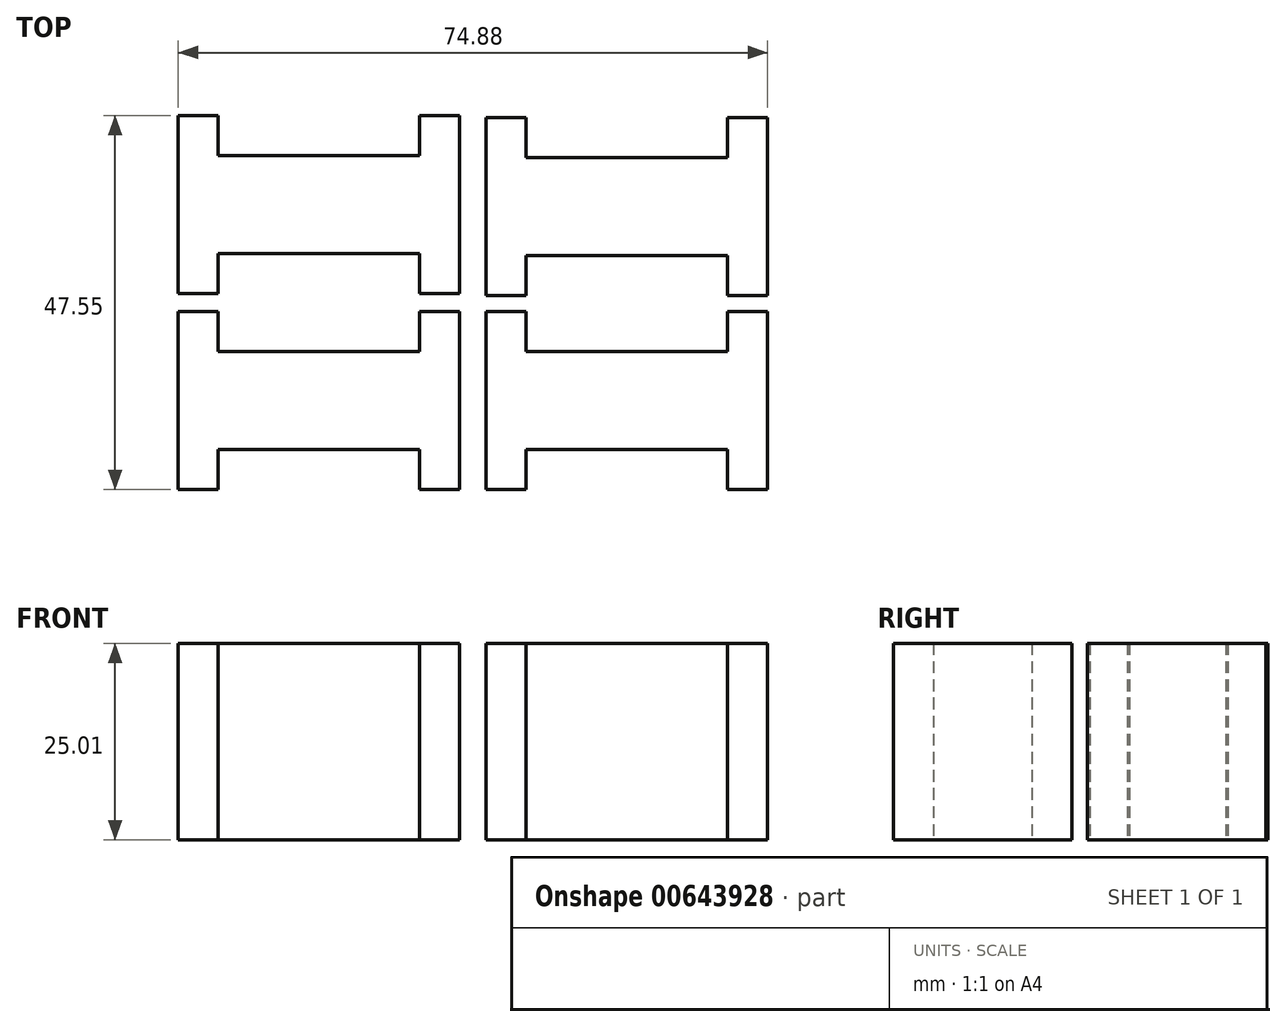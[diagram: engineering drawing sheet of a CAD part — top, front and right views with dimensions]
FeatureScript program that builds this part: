
annotation { "Feature Type Name" : "Feature", "Feature Type Description" : "" }
export const myFeature = defineFeature(function(context is Context, id is Id, definition is map)
    precondition{}
    {
        {
            var Q0;
            Q0=qCreatedBy(makeId("Top.planeOp"),FACE);
            var sketch = newSketch(context, id + "F0", { "sketchPlane" : qUnion([Q0])});
            skLineSegment(sketch, "E0.bottom", {"start": v(-12.8, 6.25) * mm, "end": v(12.8, 6.25) * mm});
            skLineSegment(sketch, "E0.top", {"start": v(-12.8, -6.25) * mm, "end": v(12.8, -6.25) * mm});
            skLineSegment(sketch, "E0.left", {"start": v(-12.8, 6.25) * mm, "end": v(-12.8, -6.25) * mm});
            skLineSegment(sketch, "E0.right", {"start": v(12.8, 6.25) * mm, "end": v(12.8, -6.25) * mm});
            skPoint(sketch, "E0.middle", {"position": v(0, 0) * mm});
            skLineSegment(sketch, "E1", {"start": v(-12.8, 6.25) * mm, "end": v(-12.8, 11.33) * mm});
            skLineSegment(sketch, "E2", {"start": v(-12.8, 11.33) * mm, "end": v(-17.88, 11.33) * mm});
            skLineSegment(sketch, "E3", {"start": v(-12.8, -6.25) * mm, "end": v(-12.8, -11.32) * mm});
            skLineSegment(sketch, "E4", {"start": v(-12.8, -11.32) * mm, "end": v(-17.88, -11.32) * mm});
            skLineSegment(sketch, "E5", {"start": v(-17.88, -11.32) * mm, "end": v(-17.88, 11.33) * mm});
            skLineSegment(sketch, "E6", {"start": v(12.8, 6.25) * mm, "end": v(12.8, 11.33) * mm});
            skLineSegment(sketch, "E7", {"start": v(12.8, 11.33) * mm, "end": v(17.88, 11.33) * mm});
            skLineSegment(sketch, "E8", {"start": v(12.8, -6.25) * mm, "end": v(12.8, -11.33) * mm});
            skLineSegment(sketch, "E9", {"start": v(12.8, -11.33) * mm, "end": v(17.88, -11.33) * mm});
            skLineSegment(sketch, "E10", {"start": v(17.88, -11.33) * mm, "end": v(17.88, 11.33) * mm});
            skSolve(sketch);
        }
        {
            var Q0;
            Q0=makeQuery(id+"F0.imprint","IMPRINT",FACE,{"disambiguationData":[TD([[makeQuery(id+"F0.imprint","IMPRINT",EDGE,{"derivedFrom":sQuery(id+"F0.wireOp",EDGE,"E0.right")}),1.0]])]});
            var Q1;
            Q1=makeQuery(id+"F0.imprint","IMPRINT",FACE,{"disambiguationData":[TD([[makeQuery(id+"F0.imprint","IMPRINT",EDGE,{"derivedFrom":sQuery(id+"F0.wireOp",EDGE,"E0.bottom")}),-1.0]])]});
            var Q2;
            Q2=makeQuery(id+"F0.imprint","IMPRINT",FACE,{"disambiguationData":[TD([[makeQuery(id+"F0.imprint","IMPRINT",EDGE,{"derivedFrom":sQuery(id+"F0.wireOp",EDGE,"E0.left")}),-1.0]])]});
            extrude(context, id + "F1", {"entities" : qUnion([Q0, Q1, Q2]), "depth" : 25 * mm, "offsetDistance" : 25.4 * mm});
        }
        {
            var Q0;
            Q0=makeQuery(id+"F1.opExtrude","SWEPT_BODY",BODY,{"disambiguationData":[OSD([sQuery(id+"F0.wireOp",EDGE,"E0.bottom"),sQuery(id+"F0.wireOp",EDGE,"E0.top"),sQuery(id+"F0.wireOp",EDGE,"E1"),sQuery(id+"F0.wireOp",EDGE,"E2"),sQuery(id+"F0.wireOp",EDGE,"E3"),sQuery(id+"F0.wireOp",EDGE,"E4"),sQuery(id+"F0.wireOp",EDGE,"E5"),sQuery(id+"F0.wireOp",EDGE,"E6"),sQuery(id+"F0.wireOp",EDGE,"E7"),sQuery(id+"F0.wireOp",EDGE,"E8"),sQuery(id+"F0.wireOp",EDGE,"E9"),sQuery(id+"F0.wireOp",EDGE,"E10")])]});
            transform(context, id + "F2", {"entities" : qUnion([Q0]), "transformType" : TransformType.TRANSLATION_3D, "dx" : 0 * mm, "dy" : 24.9 * mm, "dz" : 0 * mm, "makeCopy" : true});
        }
        {
            var Q0;
            Q0=makeQuery(id+"F1.opExtrude","SWEPT_BODY",BODY,{"disambiguationData":[OSD([sQuery(id+"F0.wireOp",EDGE,"E0.bottom"),sQuery(id+"F0.wireOp",EDGE,"E0.top"),sQuery(id+"F0.wireOp",EDGE,"E1"),sQuery(id+"F0.wireOp",EDGE,"E2"),sQuery(id+"F0.wireOp",EDGE,"E3"),sQuery(id+"F0.wireOp",EDGE,"E4"),sQuery(id+"F0.wireOp",EDGE,"E5"),sQuery(id+"F0.wireOp",EDGE,"E6"),sQuery(id+"F0.wireOp",EDGE,"E7"),sQuery(id+"F0.wireOp",EDGE,"E8"),sQuery(id+"F0.wireOp",EDGE,"E9"),sQuery(id+"F0.wireOp",EDGE,"E10")])]});
            transform(context, id + "F3", {"entities" : qUnion([Q0]), "transformType" : TransformType.TRANSLATION_3D, "dx" : 39.12 * mm, "dy" : 0 * mm, "dz" : 0 * mm, "makeCopy" : true});
        }
        {
            var Q0;
            Q0=makeQuery(id+"F2.opPattern","COPY",BODY,{"derivedFrom":makeQuery(id+"F1.opExtrude","SWEPT_BODY",BODY,{"disambiguationData":[OSD([sQuery(id+"F0.wireOp",EDGE,"E0.bottom"),sQuery(id+"F0.wireOp",EDGE,"E0.top"),sQuery(id+"F0.wireOp",EDGE,"E1"),sQuery(id+"F0.wireOp",EDGE,"E2"),sQuery(id+"F0.wireOp",EDGE,"E3"),sQuery(id+"F0.wireOp",EDGE,"E4"),sQuery(id+"F0.wireOp",EDGE,"E5"),sQuery(id+"F0.wireOp",EDGE,"E6"),sQuery(id+"F0.wireOp",EDGE,"E7"),sQuery(id+"F0.wireOp",EDGE,"E8"),sQuery(id+"F0.wireOp",EDGE,"E9"),sQuery(id+"F0.wireOp",EDGE,"E10")])]}),"instanceName":"1"});
            transform(context, id + "F4", {"entities" : qUnion([Q0]), "transformType" : TransformType.TRANSLATION_3D, "dx" : 39.12 * mm, "dy" : -0.25 * mm, "dz" : 0 * mm, "makeCopy" : true});
        }
    });
